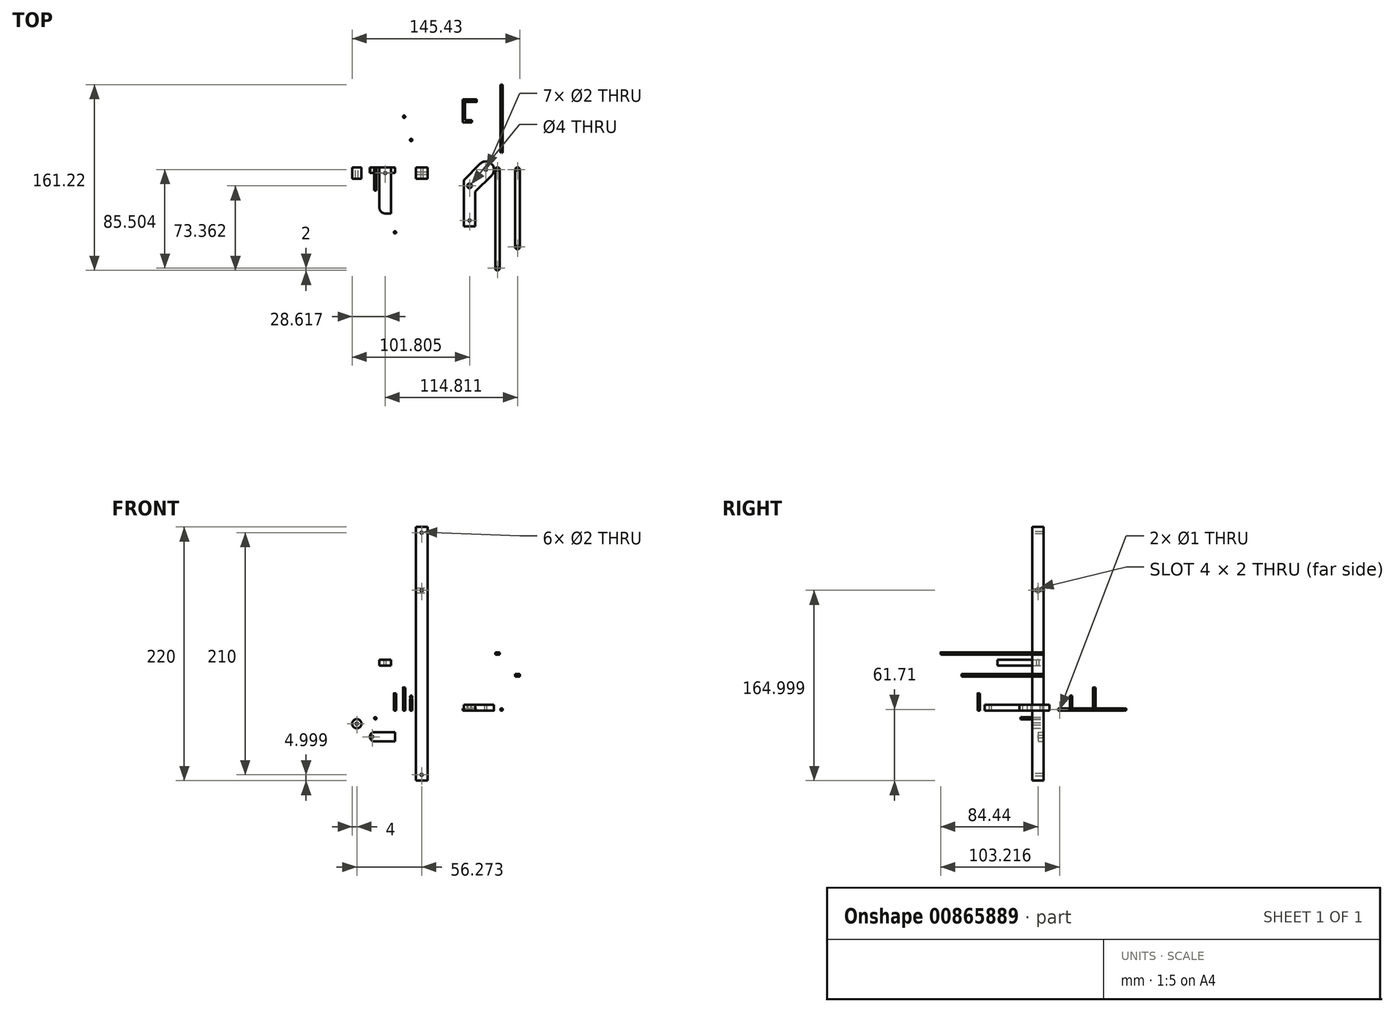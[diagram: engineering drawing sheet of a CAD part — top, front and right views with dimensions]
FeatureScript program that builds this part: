
annotation { "Feature Type Name" : "Feature", "Feature Type Description" : "" }
export const myFeature = defineFeature(function(context is Context, id is Id, definition is map)
    precondition{}
    {
        {
            var Q0;
            Q0=qCreatedBy(makeId("Front.planeOp"),FACE);
            var sketch = newSketch(context, id + "F0", { "sketchPlane" : qUnion([Q0])});
            skLineSegment(sketch, "E0.bottom", {"start": v(-64.11, 44.14) * mm, "end": v(-54.11, 44.14) * mm});
            skLineSegment(sketch, "E0.top", {"start": v(-64.11, 39.14) * mm, "end": v(-54.11, 39.14) * mm});
            skLineSegment(sketch, "E0.left", {"start": v(-64.11, 44.14) * mm, "end": v(-64.11, 39.14) * mm});
            skLineSegment(sketch, "E0.right", {"start": v(-54.11, 44.14) * mm, "end": v(-54.11, 39.14) * mm});
            skSolve(sketch);
        }
        {
            var Q0;
            Q0=qSketchRegion(id+"F0",true);
            extrude(context, id + "F1", {"entities" : qUnion([Q0]), "depth" : 40 * mm, "offsetDistance" : 25 * mm});
        }
        {
            var Q0;
            Q0=makeQuery(id+"F1.opExtrude","CAP_EDGE",EDGE,{"disambiguationData":[OSD([sQuery(id+"F0.wireOp",EDGE,"E0.left")])],"isStart":false});
            fillet(context, id + "F2", {"entities" : qUnion([Q0]), "radius" : 5 * mm, "tangentPropagation" : true, "allowEdgeOverflow" : false});
        }
        {
            var Q0;
            Q0=makeQuery(id+"F1.opExtrude","SWEPT_FACE",FACE,{"disambiguationData":[OSD([sQuery(id+"F0.wireOp",EDGE,"E0.bottom")])]});
            var sketch = newSketch(context, id + "F3", { "sketchPlane" : qUnion([Q0])});
            skCircle(sketch, "E1", {"center": v(-59.11, -5) * mm, "radius": 1 * mm});
            skPoint(sketch, "E1.centerSnap0", {"position": v(-59.11, 0) * mm});
            skSolve(sketch);
        }
        {
            var Q0;
            Q0=qSketchRegion(id+"F3",true);
            extrude(context, id + "F4", {"entities" : qUnion([Q0]), "operationType" : NewBodyOperationType.REMOVE, "oppositeDirection" : true, "depth" : 10 * mm, "offsetDistance" : 25 * mm});
        }
        {
            var Q0;
            Q0=qCreatedBy(makeId("Top.planeOp"),FACE);
            var sketch = newSketch(context, id + "F5", { "sketchPlane" : qUnion([Q0])});
            skLineSegment(sketch, "E2", {"start": v(9.07, -11.08) * mm, "end": v(9.07, -51.08) * mm});
            skLineSegment(sketch, "E3", {"start": v(9.07, -51.08) * mm, "end": v(19.07, -51.08) * mm});
            skLineSegment(sketch, "E4", {"start": v(19.07, -51.08) * mm, "end": v(19.07, -21.08) * mm});
            skLineSegment(sketch, "E5.bottom", {"start": v(9.07, -11.08) * mm, "end": v(19.07, -21.08) * mm});
            skLineSegment(sketch, "E5.top", {"start": v(23.22, 3.06) * mm, "end": v(33.22, -6.94) * mm});
            skLineSegment(sketch, "E5.left", {"start": v(23.22, 3.06) * mm, "end": v(9.07, -11.08) * mm});
            skLineSegment(sketch, "E5.right", {"start": v(33.22, -6.94) * mm, "end": v(19.07, -21.08) * mm});
            skCircle(sketch, "E6", {"center": v(28.22, -1.94) * mm, "radius": 7.07 * mm});
            skSolve(sketch);
        }
        {
            var Q0;
            Q0=qSketchRegion(id+"F5",true);
            extrude(context, id + "F6", {"entities" : qUnion([Q0]), "depth" : 5 * mm, "offsetDistance" : 25 * mm});
        }
        {
            var Q0;
            Q0=makeQuery(id+"F6.opExtrude","CAP_FACE",FACE,{"disambiguationData":[OSD([sQuery(id+"F5.wireOp",EDGE,"E2"),sQuery(id+"F5.wireOp",EDGE,"E3"),sQuery(id+"F5.wireOp",EDGE,"E4"),sQuery(id+"F5.wireOp",EDGE,"E5.left"),sQuery(id+"F5.wireOp",EDGE,"E5.right"),sQuery(id+"F5.wireOp",EDGE,"E6")])],"isStart":false});
            var sketch = newSketch(context, id + "F7", { "sketchPlane" : qUnion([Q0])});
            skCircle(sketch, "E7", {"center": v(14.07, -16.08) * mm, "radius": 2 * mm});
            skCircle(sketch, "E8", {"center": v(28.22, -1.94) * mm, "radius": 1 * mm});
            skSolve(sketch);
        }
        {
            var Q0;
            Q0=qSketchRegion(id+"F7",true);
            extrude(context, id + "F8", {"entities" : qUnion([Q0]), "operationType" : NewBodyOperationType.REMOVE, "endBound" : BoundingType.THROUGH_ALL, "oppositeDirection" : true, "depth" : 25 * mm, "offsetDistance" : 25 * mm});
        }
        {
            var Q0;
            Q0=makeQuery(id+"F6.opExtrude","CAP_FACE",FACE,{"disambiguationData":[OSD([sQuery(id+"F5.wireOp",EDGE,"E2"),sQuery(id+"F5.wireOp",EDGE,"E3"),sQuery(id+"F5.wireOp",EDGE,"E4"),sQuery(id+"F5.wireOp",EDGE,"E5.left"),sQuery(id+"F5.wireOp",EDGE,"E5.right"),sQuery(id+"F5.wireOp",EDGE,"E6")])],"isStart":false});
            var sketch = newSketch(context, id + "F9", { "sketchPlane" : qUnion([Q0])});
            skCircle(sketch, "E9", {"center": v(14.07, -46.08) * mm, "radius": 1 * mm});
            skPoint(sketch, "E9.centerSnap0", {"position": v(14.07, -51.08) * mm});
            skSolve(sketch);
        }
        {
            var Q0;
            Q0=qSketchRegion(id+"F9",true);
            extrude(context, id + "F10", {"entities" : qUnion([Q0]), "operationType" : NewBodyOperationType.REMOVE, "oppositeDirection" : true, "depth" : 10 * mm, "offsetDistance" : 25 * mm});
        }
        {
            var Q0;
            Q0=qCreatedBy(makeId("Front.planeOp"),FACE);
            var sketch = newSketch(context, id + "F11", { "sketchPlane" : qUnion([Q0])});
            skLineSegment(sketch, "E10.bottom", {"start": v(-32.46, 159.29) * mm, "end": v(-22.46, 159.29) * mm});
            skLineSegment(sketch, "E10.top", {"start": v(-32.46, -60.71) * mm, "end": v(-22.46, -60.71) * mm});
            skLineSegment(sketch, "E10.left", {"start": v(-32.46, 159.29) * mm, "end": v(-32.46, -60.71) * mm});
            skLineSegment(sketch, "E10.right", {"start": v(-22.46, 159.29) * mm, "end": v(-22.46, -60.71) * mm});
            skSolve(sketch);
        }
        {
            var Q0;
            Q0=qSketchRegion(id+"F11",true);
            extrude(context, id + "F12", {"entities" : qUnion([Q0]), "depth" : 10 * mm, "offsetDistance" : 25 * mm});
        }
        {
            var Q0;
            Q0=makeQuery(id+"F12.opExtrude","CAP_FACE",FACE,{"disambiguationData":[OSD([sQuery(id+"F11.wireOp",EDGE,"E10.bottom"),sQuery(id+"F11.wireOp",EDGE,"E10.top"),sQuery(id+"F11.wireOp",EDGE,"E10.left"),sQuery(id+"F11.wireOp",EDGE,"E10.right"),sQuery(id+"F11.wireOp",EDGE,"ZyOirPLE-tay3-UPC8-JogP-EygBYQC14ixe"),sQuery(id+"F11.wireOp",EDGE,"AGVEhOqr-N9d4-Yz4L-8zqB-sNM6V8mEr66d")])],"isStart":false});
            var sketch = newSketch(context, id + "F13", { "sketchPlane" : qUnion([Q0])});
            skCircle(sketch, "E11", {"center": v(-27.46, 154.29) * mm, "radius": 1 * mm});
            skCircle(sketch, "E12", {"center": v(-27.46, 104.29) * mm, "radius": 1 * mm});
            skSolve(sketch);
        }
        {
            var Q0;
            Q0=qSketchRegion(id+"F13",true);
            extrude(context, id + "F14", {"entities" : qUnion([Q0]), "operationType" : NewBodyOperationType.REMOVE, "endBound" : BoundingType.THROUGH_ALL, "oppositeDirection" : true, "depth" : 25 * mm, "offsetDistance" : 25 * mm});
        }
        {
            var Q0;
            Q0=makeQuery(id+"F12.opExtrude","CAP_FACE",FACE,{"disambiguationData":[OSD([sQuery(id+"F11.wireOp",EDGE,"E10.bottom"),sQuery(id+"F11.wireOp",EDGE,"E10.top"),sQuery(id+"F11.wireOp",EDGE,"E10.left"),sQuery(id+"F11.wireOp",EDGE,"E10.right"),sQuery(id+"F11.wireOp",EDGE,"ZyOirPLE-tay3-UPC8-JogP-EygBYQC14ixe"),sQuery(id+"F11.wireOp",EDGE,"AGVEhOqr-N9d4-Yz4L-8zqB-sNM6V8mEr66d")])],"isStart":false});
            var sketch = newSketch(context, id + "F15", { "sketchPlane" : qUnion([Q0])});
            skCircle(sketch, "E13", {"center": v(-27.46, -55.71) * mm, "radius": 1 * mm});
            skPoint(sketch, "E13.centerSnap0", {"position": v(-27.46, -60.71) * mm});
            skSolve(sketch);
        }
        {
            var Q0;
            Q0=qSketchRegion(id+"F15",true);
            extrude(context, id + "F16", {"entities" : qUnion([Q0]), "operationType" : NewBodyOperationType.REMOVE, "endBound" : BoundingType.THROUGH_ALL, "oppositeDirection" : true, "depth" : 5 * mm, "offsetDistance" : 50 * mm});
        }
        {
            var Q0;
            Q0=qCreatedBy(makeId("Top.planeOp"),FACE);
            var sketch = newSketch(context, id + "F17", { "sketchPlane" : qUnion([Q0])});
            skCircle(sketch, "E14", {"center": v(-42.7, 43.9) * mm, "radius": 1 * mm});
            skSolve(sketch);
        }
        {
            var Q0;
            Q0=qSketchRegion(id+"F17",true);
            extrude(context, id + "F18", {"entities" : qUnion([Q0]), "depth" : 20 * mm, "offsetDistance" : 25 * mm});
        }
        {
            var Q0;
            Q0=qCreatedBy(makeId("Front.planeOp"),FACE);
            var sketch = newSketch(context, id + "F19", { "sketchPlane" : qUnion([Q0])});
            skLineSegment(sketch, "E15.bottom", {"start": v(36.33, 50.54) * mm, "end": v(40.33, 50.54) * mm});
            skLineSegment(sketch, "E15.top", {"start": v(36.33, 48.54) * mm, "end": v(40.33, 48.54) * mm});
            skLineSegment(sketch, "E15.left", {"start": v(36.33, 50.54) * mm, "end": v(36.33, 48.54) * mm});
            skLineSegment(sketch, "E15.right", {"start": v(40.33, 50.54) * mm, "end": v(40.33, 48.54) * mm});
            skSolve(sketch);
        }
        {
            var Q0;
            Q0 = qSketchRegion(id + "F19", true);
            extrude(context, id + "F20", {"entities" : qUnion([Q0]), "depth" : 89.44 * mm, "offsetDistance" : 25 * mm});
        }
        {
            var Q0;
            Q0=makeQuery(id+"F20.opExtrude","SWEPT_FACE",FACE,{"disambiguationData":[OSD([sQuery(id+"F19.wireOp",EDGE,"E15.bottom")])]});
            var sketch = newSketch(context, id + "F21", { "sketchPlane" : qUnion([Q0])});
            skCircle(sketch, "E16", {"center": v(38.33, -2) * mm, "radius": 1 * mm});
            skPoint(sketch, "E16.centerSnap0", {"position": v(38.33, 0) * mm});
            skCircle(sketch, "E17", {"center": v(38.33, -87.44) * mm, "radius": 1 * mm});
            skPoint(sketch, "E17.centerSnap0", {"position": v(38.33, -89.44) * mm});
            skSolve(sketch);
        }
        {
            var Q0;
            Q0 = qSketchRegion(id + "F21", true);
            extrude(context, id + "F22", {"entities" : qUnion([Q0]), "operationType" : NewBodyOperationType.REMOVE, "endBound" : BoundingType.THROUGH_ALL, "oppositeDirection" : true, "depth" : 25 * mm, "offsetDistance" : 25 * mm});
        }
        {
            var Q0;
            Q0=makeQuery(id+"F20.opExtrude","CAP_EDGE",EDGE,{"disambiguationData":[OSD([sQuery(id+"F19.wireOp",EDGE,"E15.left")])],"isStart":false});
            var Q1;
            Q1=makeQuery(id+"F20.opExtrude","CAP_EDGE",EDGE,{"disambiguationData":[OSD([sQuery(id+"F19.wireOp",EDGE,"E15.right")])],"isStart":false});
            var Q2;
            Q2=makeQuery(id+"F20.opExtrude","CAP_EDGE",EDGE,{"disambiguationData":[OSD([sQuery(id+"F19.wireOp",EDGE,"E15.right")])],"isStart":true});
            var Q3;
            Q3=makeQuery(id+"F20.opExtrude","CAP_EDGE",EDGE,{"disambiguationData":[OSD([sQuery(id+"F19.wireOp",EDGE,"E15.left")])],"isStart":true});
            fillet(context, id + "F23", {"entities" : qUnion([Q0, Q1, Q2, Q3]), "radius" : 2 * mm, "tangentPropagation" : true, "allowEdgeOverflow" : false});
        }
        {
            var Q0;
            Q0=qCreatedBy(makeId("Front.planeOp"),FACE);
            var sketch = newSketch(context, id + "F24", { "sketchPlane" : qUnion([Q0])});
            skLineSegment(sketch, "E18.bottom", {"start": v(53.7, 31.66) * mm, "end": v(57.7, 31.66) * mm});
            skLineSegment(sketch, "E18.top", {"start": v(53.7, 29.66) * mm, "end": v(57.7, 29.66) * mm});
            skLineSegment(sketch, "E18.left", {"start": v(53.7, 31.66) * mm, "end": v(53.7, 29.66) * mm});
            skLineSegment(sketch, "E18.right", {"start": v(57.7, 31.66) * mm, "end": v(57.7, 29.66) * mm});
            skSolve(sketch);
        }
        {
            var Q0;
            Q0 = qSketchRegion(id + "F24", true);
            extrude(context, id + "F25", {"entities" : qUnion([Q0]), "depth" : 71.08 * mm, "offsetDistance" : 25 * mm});
        }
        {
            var Q0;
            Q0=makeQuery(id+"F25.opExtrude","SWEPT_FACE",FACE,{"disambiguationData":[OSD([sQuery(id+"F24.wireOp",EDGE,"E18.bottom")])]});
            var sketch = newSketch(context, id + "F26", { "sketchPlane" : qUnion([Q0])});
            skCircle(sketch, "E19", {"center": v(55.7, -2) * mm, "radius": 1 * mm});
            skPoint(sketch, "E19.centerSnap0", {"position": v(55.7, 0) * mm});
            skCircle(sketch, "E20", {"center": v(55.7, -69.08) * mm, "radius": 1 * mm});
            skPoint(sketch, "E20.centerSnap0", {"position": v(55.7, -71.08) * mm});
            skSolve(sketch);
        }
        {
            var Q0;
            Q0 = qSketchRegion(id + "F26", true);
            extrude(context, id + "F27", {"entities" : qUnion([Q0]), "operationType" : NewBodyOperationType.REMOVE, "endBound" : BoundingType.THROUGH_ALL, "oppositeDirection" : true, "depth" : 25 * mm, "offsetDistance" : 25 * mm});
        }
        {
            var Q0;
            Q0=makeQuery(id+"F25.opExtrude","CAP_EDGE",EDGE,{"disambiguationData":[OSD([sQuery(id+"F24.wireOp",EDGE,"E18.right")])],"isStart":true});
            var Q1;
            Q1=makeQuery(id+"F25.opExtrude","CAP_EDGE",EDGE,{"disambiguationData":[OSD([sQuery(id+"F24.wireOp",EDGE,"E18.left")])],"isStart":true});
            var Q2;
            Q2=makeQuery(id+"F25.opExtrude","CAP_EDGE",EDGE,{"disambiguationData":[OSD([sQuery(id+"F24.wireOp",EDGE,"E18.right")])],"isStart":false});
            var Q3;
            Q3=makeQuery(id+"F25.opExtrude","CAP_EDGE",EDGE,{"disambiguationData":[OSD([sQuery(id+"F24.wireOp",EDGE,"E18.left")])],"isStart":false});
            fillet(context, id + "F28", {"entities" : qUnion([Q0, Q1, Q2, Q3]), "radius" : 2 * mm, "tangentPropagation" : true, "allowEdgeOverflow" : false});
        }
        {
            var Q0;
            Q0=qCreatedBy(makeId("Top.planeOp"),FACE);
            var sketch = newSketch(context, id + "F29", { "sketchPlane" : qUnion([Q0])});
            skLineSegment(sketch, "E21.bottom", {"start": v(8.26, 58.82) * mm, "end": v(10.26, 58.82) * mm});
            skLineSegment(sketch, "E21.top", {"start": v(8.26, 38.82) * mm, "end": v(10.26, 38.82) * mm});
            skLineSegment(sketch, "E21.left", {"start": v(8.26, 58.82) * mm, "end": v(8.26, 38.82) * mm});
            skLineSegment(sketch, "E21.right", {"start": v(10.26, 58.82) * mm, "end": v(10.26, 38.82) * mm});
            skLineSegment(sketch, "E22.bottom", {"start": v(10.26, 40.82) * mm, "end": v(16.26, 40.82) * mm});
            skLineSegment(sketch, "E22.top", {"start": v(10.26, 38.82) * mm, "end": v(16.26, 38.82) * mm});
            skLineSegment(sketch, "E22.left", {"start": v(10.26, 40.82) * mm, "end": v(10.26, 38.82) * mm});
            skLineSegment(sketch, "E22.right", {"start": v(16.26, 40.82) * mm, "end": v(16.26, 38.82) * mm});
            skLineSegment(sketch, "E23.bottom", {"start": v(40.76, 69.78) * mm, "end": v(42.76, 69.78) * mm});
            skLineSegment(sketch, "E23.top", {"start": v(40.76, 12.78) * mm, "end": v(42.76, 12.78) * mm});
            skLineSegment(sketch, "E23.left", {"start": v(40.76, 69.78) * mm, "end": v(40.76, 12.78) * mm});
            skLineSegment(sketch, "E23.right", {"start": v(42.76, 69.78) * mm, "end": v(42.76, 12.78) * mm});
            skSolve(sketch);
        }
        {
            var Q0;
            Q0 = qSketchRegion(id + "F29", true);
            extrude(context, id + "F30", {"entities" : qUnion([Q0]), "depth" : 2 * mm, "offsetDistance" : 25 * mm});
        }
        {
            var Q0;
            Q0=makeQuery(id+"F30.opExtrude","SWEPT_FACE",FACE,{"disambiguationData":[OSD([sQuery(id+"F29.wireOp",EDGE,"E21.right")])]});
            var sketch = newSketch(context, id + "F31", { "sketchPlane" : qUnion([Q0])});
            skCircle(sketch, "E24", {"center": v(57.82, 1) * mm, "radius": 1 * mm});
            skPoint(sketch, "E24.centerSnap0", {"position": v(58.82, 1) * mm});
            skSolve(sketch);
        }
        {
            var Q0;
            Q0 = qSketchRegion(id + "F31", true);
            extrude(context, id + "F32", {"entities" : qUnion([Q0]), "operationType" : NewBodyOperationType.ADD, "depth" : 10 * mm, "offsetDistance" : 25 * mm});
        }
        {
            var Q0;
            Q0=qCreatedBy(makeId("Top.planeOp"),FACE);
            var sketch = newSketch(context, id + "F33", { "sketchPlane" : qUnion([Q0])});
            skCircle(sketch, "E25", {"center": v(-36.55, 23.7) * mm, "radius": 1 * mm});
            skSolve(sketch);
        }
        {
            var Q0;
            Q0 = qSketchRegion(id + "F33", true);
            extrude(context, id + "F34", {"entities" : qUnion([Q0]), "depth" : 10 * mm, "offsetDistance" : 25 * mm});
        }
        {
            var Q0;
            Q0=makeQuery(id+"F34.opExtrude","CAP_FACE",FACE,{"disambiguationData":[OSD([sQuery(id+"F33.wireOp",EDGE,"E25")])],"isStart":false});
            var sketch = newSketch(context, id + "F35", { "sketchPlane" : qUnion([Q0])});
            skLineSegment(sketch, "E26.bottom", {"start": v(-37.05, 24.57) * mm, "end": v(-36.05, 24.57) * mm});
            skLineSegment(sketch, "E26.top", {"start": v(-37.05, 22.84) * mm, "end": v(-36.05, 22.84) * mm});
            skLineSegment(sketch, "E26.left", {"start": v(-37.05, 24.57) * mm, "end": v(-37.05, 22.84) * mm});
            skLineSegment(sketch, "E26.right", {"start": v(-36.05, 24.57) * mm, "end": v(-36.05, 22.84) * mm});
            skSolve(sketch);
        }
        {
            var Q0;
            Q0 = qSketchRegion(id + "F35", true);
            extrude(context, id + "F36", {"entities" : qUnion([Q0]), "operationType" : NewBodyOperationType.ADD, "depth" : 3 * mm, "offsetDistance" : 25 * mm});
        }
        {
            var Q0;
            Q0=makeQuery(id+"F36.opExtrude","SWEPT_FACE",FACE,{"disambiguationData":[OSD([sQuery(id+"F35.wireOp",EDGE,"E26.left")])]});
            var sketch = newSketch(context, id + "F37", { "sketchPlane" : qUnion([Q0])});
            skCircle(sketch, "E27", {"center": v(-23.7, 12) * mm, "radius": 0.5 * mm});
            skPoint(sketch, "E27.centerSnap0", {"position": v(-23.7, 13) * mm});
            skSolve(sketch);
        }
        {
            var Q0;
            Q0 = qSketchRegion(id + "F37", true);
            extrude(context, id + "F38", {"entities" : qUnion([Q0]), "operationType" : NewBodyOperationType.ADD, "depth" : 0.5 * mm, "offsetDistance" : 25 * mm, "hasSecondDirection" : true, "secondDirectionOppositeDirection" : true, "secondDirectionDepth" : 1.5 * mm});
        }
        {
            var Q0;
            Q0=makeQuery(id+"F30.opExtrude","SWEPT_FACE",FACE,{"disambiguationData":[OSD([sQuery(id+"F29.wireOp",EDGE,"E22.right")])]});
            var sketch = newSketch(context, id + "F39", { "sketchPlane" : qUnion([Q0])});
            skLineSegment(sketch, "E28.bottom", {"start": v(40.82, 1.5) * mm, "end": v(38.82, 1.5) * mm});
            skLineSegment(sketch, "E28.top", {"start": v(40.82, 0.5) * mm, "end": v(38.82, 0.5) * mm});
            skLineSegment(sketch, "E28.left", {"start": v(40.82, 1.5) * mm, "end": v(40.82, 0.5) * mm});
            skLineSegment(sketch, "E28.right", {"start": v(38.82, 1.5) * mm, "end": v(38.82, 0.5) * mm});
            skSolve(sketch);
        }
        {
            var Q0;
            Q0 = qSketchRegion(id + "F39", true);
            extrude(context, id + "F40", {"entities" : qUnion([Q0]), "operationType" : NewBodyOperationType.REMOVE, "oppositeDirection" : true, "depth" : 3 * mm, "offsetDistance" : 25 * mm});
        }
        {
            var Q0;
            Q0=makeQuery(id+"F30.opExtrude","CAP_FACE",FACE,{"disambiguationData":[OSD([sQuery(id+"F29.wireOp",EDGE,"E21.bottom"),sQuery(id+"F29.wireOp",EDGE,"E21.top"),sQuery(id+"F29.wireOp",EDGE,"E21.left"),sQuery(id+"F29.wireOp",EDGE,"E21.right"),sQuery(id+"F29.wireOp",EDGE,"E22.bottom"),sQuery(id+"F29.wireOp",EDGE,"E22.top"),sQuery(id+"F29.wireOp",EDGE,"E22.right")])],"isStart":false});
            var sketch = newSketch(context, id + "F41", { "sketchPlane" : qUnion([Q0])});
            skCircle(sketch, "E29", {"center": v(15.26, 39.82) * mm, "radius": 0.5 * mm});
            skPoint(sketch, "E29.centerSnap0", {"position": v(16.26, 39.82) * mm});
            skSolve(sketch);
        }
        {
            var Q0;
            Q0 = qSketchRegion(id + "F41", true);
            extrude(context, id + "F42", {"entities" : qUnion([Q0]), "operationType" : NewBodyOperationType.REMOVE, "endBound" : BoundingType.THROUGH_ALL, "oppositeDirection" : true, "depth" : 25 * mm, "offsetDistance" : 25 * mm});
        }
        {
            var Q0;
            Q0=makeQuery(id+"F30.opExtrude","SWEPT_FACE",FACE,{"disambiguationData":[OSD([sQuery(id+"F29.wireOp",EDGE,"E23.bottom")])]});
            var sketch = newSketch(context, id + "F43", { "sketchPlane" : qUnion([Q0])});
            skLineSegment(sketch, "E30.bottom", {"start": v(-40.76, 0.5) * mm, "end": v(-42.76, 0.5) * mm});
            skLineSegment(sketch, "E30.top", {"start": v(-40.76, 1.5) * mm, "end": v(-42.76, 1.5) * mm});
            skLineSegment(sketch, "E30.left", {"start": v(-40.76, 0.5) * mm, "end": v(-40.76, 1.5) * mm});
            skLineSegment(sketch, "E30.right", {"start": v(-42.76, 0.5) * mm, "end": v(-42.76, 1.5) * mm});
            skSolve(sketch);
        }
        {
            var Q0;
            Q0 = qSketchRegion(id + "F43", true);
            extrude(context, id + "F44", {"entities" : qUnion([Q0]), "operationType" : NewBodyOperationType.ADD, "depth" : 2 * mm, "offsetDistance" : 25 * mm});
        }
        {
            var Q0;
            Q0=makeQuery(id+"F44.opExtrude","SWEPT_FACE",FACE,{"disambiguationData":[OSD([sQuery(id+"F43.wireOp",EDGE,"E30.bottom")])]});
            var sketch = newSketch(context, id + "F45", { "sketchPlane" : qUnion([Q0])});
            skCircle(sketch, "E31", {"center": v(41.76, -70.78) * mm, "radius": 0.5 * mm});
            skPoint(sketch, "E31.centerSnap0", {"position": v(41.76, -71.78) * mm});
            skSolve(sketch);
        }
        {
            var Q0;
            Q0 = qSketchRegion(id + "F45", true);
            extrude(context, id + "F46", {"entities" : qUnion([Q0]), "operationType" : NewBodyOperationType.ADD, "depth" : 0.5 * mm, "offsetDistance" : 25 * mm, "hasSecondDirection" : true, "secondDirectionOppositeDirection" : true, "secondDirectionDepth" : 1.5 * mm});
        }
        {
            var Q0;
            Q0=makeQuery(id+"F30.opExtrude","SWEPT_FACE",FACE,{"disambiguationData":[OSD([sQuery(id+"F29.wireOp",EDGE,"E23.top")])]});
            var sketch = newSketch(context, id + "F47", { "sketchPlane" : qUnion([Q0])});
            skLineSegment(sketch, "E32.bottom", {"start": v(41.26, 2) * mm, "end": v(42.26, 2) * mm});
            skLineSegment(sketch, "E32.top", {"start": v(41.26, 0) * mm, "end": v(42.26, 0) * mm});
            skLineSegment(sketch, "E32.left", {"start": v(41.26, 2) * mm, "end": v(41.26, 0) * mm});
            skLineSegment(sketch, "E32.right", {"start": v(42.26, 2) * mm, "end": v(42.26, 0) * mm});
            skSolve(sketch);
        }
        {
            var Q0;
            Q0 = qSketchRegion(id + "F47", true);
            extrude(context, id + "F48", {"entities" : qUnion([Q0]), "operationType" : NewBodyOperationType.REMOVE, "oppositeDirection" : true, "depth" : 3 * mm, "offsetDistance" : 25 * mm});
        }
        {
            var Q0;
            Q0=makeQuery(id+"F44.boolean.opBoolean","MERGE",FACE,{"derivedFrom":[makeQuery(id+"F30.opExtrude","SWEPT_FACE",FACE,{"disambiguationData":[OSD([sQuery(id+"F29.wireOp",EDGE,"E23.right")])]}),makeQuery(id+"F44.opExtrude","SWEPT_FACE",FACE,{"disambiguationData":[OSD([sQuery(id+"F43.wireOp",EDGE,"E30.right")])]})]});
            var sketch = newSketch(context, id + "F49", { "sketchPlane" : qUnion([Q0])});
            skCircle(sketch, "E33", {"center": v(13.78, 1) * mm, "radius": 0.5 * mm});
            skPoint(sketch, "E33.centerSnap0", {"position": v(12.78, 1) * mm});
            skSolve(sketch);
        }
        {
            var Q0;
            Q0 = qSketchRegion(id + "F49", true);
            extrude(context, id + "F50", {"entities" : qUnion([Q0]), "operationType" : NewBodyOperationType.REMOVE, "endBound" : BoundingType.THROUGH_ALL, "oppositeDirection" : true, "depth" : 25 * mm, "offsetDistance" : 25 * mm});
        }
        {
            var Q0;
            Q0=qCreatedBy(makeId("Front.planeOp"),FACE);
            var sketch = newSketch(context, id + "F51", { "sketchPlane" : qUnion([Q0])});
            skLineSegment(sketch, "E34", {"start": v(-70.38, -18.72) * mm, "end": v(-50.38, -18.72) * mm});
            skLineSegment(sketch, "E35", {"start": v(-50.38, -18.72) * mm, "end": v(-50.38, -26.72) * mm});
            skLineSegment(sketch, "E36", {"start": v(-50.38, -26.72) * mm, "end": v(-70.38, -26.72) * mm});
            skArc(sketch, "E37", {"start": v(-68.38, -18.72) * mm, "mid": v(-72.38, -22.72) * mm, "end": v(-68.38, -26.72) * mm});
            skSolve(sketch);
        }
        {
            var Q0;
            Q0 = qSketchRegion(id + "F51", true);
            extrude(context, id + "F52", {"entities" : qUnion([Q0]), "depth" : 5 * mm, "offsetDistance" : 25 * mm});
        }
        {
            var Q0;
            Q0=makeQuery(id+"F52.opExtrude","CAP_FACE",FACE,{"disambiguationData":[OSD([sQuery(id+"F51.wireOp",EDGE,"E34"),sQuery(id+"F51.wireOp",EDGE,"E35"),sQuery(id+"F51.wireOp",EDGE,"E36"),sQuery(id+"F51.wireOp",EDGE,"E37")])],"isStart":false});
            var sketch = newSketch(context, id + "F53", { "sketchPlane" : qUnion([Q0])});
            skCircle(sketch, "E38", {"center": v(-70.38, -22.72) * mm, "radius": 1 * mm});
            skSolve(sketch);
        }
        {
            var Q0;
            Q0 = qSketchRegion(id + "F53", true);
            extrude(context, id + "F54", {"entities" : qUnion([Q0]), "operationType" : NewBodyOperationType.REMOVE, "endBound" : BoundingType.THROUGH_ALL, "oppositeDirection" : true, "depth" : 25 * mm, "offsetDistance" : 25 * mm});
        }
        {
            var Q0;
            Q0=qCreatedBy(makeId("Front.planeOp"),FACE);
            var sketch = newSketch(context, id + "F55", { "sketchPlane" : qUnion([Q0])});
            skCircle(sketch, "E39", {"center": v(-67.6, -6.65) * mm, "radius": 1 * mm});
            skSolve(sketch);
        }
        {
            var Q0;
            Q0 = qSketchRegion(id + "F55", true);
            extrude(context, id + "F56", {"entities" : qUnion([Q0]), "depth" : 20 * mm, "offsetDistance" : 25 * mm});
        }
        {
            var Q0;
            Q0=qCreatedBy(makeId("Front.planeOp"),FACE);
            var sketch = newSketch(context, id + "F57", { "sketchPlane" : qUnion([Q0])});
            skCircle(sketch, "E40", {"center": v(-83.73, -11.36) * mm, "radius": 4 * mm});
            skCircle(sketch, "E41", {"center": v(-83.73, -11.36) * mm, "radius": 1 * mm});
            skSolve(sketch);
        }
        {
            var Q0;
            Q0 = qSketchRegion(id + "F57", true);
            extrude(context, id + "F58", {"entities" : qUnion([Q0]), "depth" : 10 * mm, "offsetDistance" : 25 * mm});
        }
        {
            var Q0;
            Q0=makeQuery(id+"F12.opExtrude","SWEPT_FACE",FACE,{"disambiguationData":[OSD([sQuery(id+"F11.wireOp",EDGE,"E10.right")])]});
            var sketch = newSketch(context, id + "F59", { "sketchPlane" : qUnion([Q0])});
            skArc(sketch, "E42", {"start": v(-4, 105.29) * mm, "mid": v(-5, 106.29) * mm, "end": v(-6, 105.29) * mm});
            skPoint(sketch, "E43", {"position": v(-5, 159.29) * mm});
            skArc(sketch, "E44", {"start": v(-6, 103.29) * mm, "mid": v(-5, 102.29) * mm, "end": v(-4, 103.29) * mm});
            skLineSegment(sketch, "E45", {"start": v(-6, 105.29) * mm, "end": v(-6, 103.29) * mm});
            skLineSegment(sketch, "E46", {"start": v(-4, 105.29) * mm, "end": v(-4, 103.29) * mm});
            skSolve(sketch);
        }
        {
            var Q0;
            Q0 = qSketchRegion(id + "F59", true);
            extrude(context, id + "F60", {"entities" : qUnion([Q0]), "operationType" : NewBodyOperationType.REMOVE, "oppositeDirection" : true, "depth" : 25 * mm, "offsetDistance" : 25 * mm});
        }
        {
            var Q0;
            Q0=qCreatedBy(makeId("Top.planeOp"),FACE);
            var sketch = newSketch(context, id + "F61", { "sketchPlane" : qUnion([Q0])});
            skCircle(sketch, "E47", {"center": v(-50.6, -56.39) * mm, "radius": 1 * mm});
            skSolve(sketch);
        }
        {
            var Q0;
            Q0 = qSketchRegion(id + "F61", true);
            extrude(context, id + "F62", {"entities" : qUnion([Q0]), "depth" : 15 * mm, "offsetDistance" : 25 * mm});
        }
    });
